# Revit family: ВУТР ПЕ_Eng
name_source: partatom
category: Mechanical Equipment
units: mm (PartAtom-declared; Revit-internal decimal feet)

## family parameters
Always vertical = Yes
Classification = None
Cut with Voids When Loaded = No
Part Type = Normal
Room Calculation Point = No
Round Connector Dimension = Use Diameter
Shared = No
Work Plane-Based = No

## types (20) — shared parameters
00_20_Manufacturer = Vents
00_20_Name = Air handling unit
An = 120 mm  [stored 0.393701 ft]
Casing Material = Steel, galvanized
D1 = 125 mm  [stored 0.410105 ft]
D1y = 120 mm  [stored 0.393701 ft]
Description = Heat- and sound-insulated casing
Filter = G4/G4, F7
Frequency = 50 Hz
Hz = 113 mm
Load Classification = HVAC
Maintenance zone material = <By Category>
Manufacturer = Vents
Number of Fase = 1
Temperature of moving air = -25...+40 °C
URL = https://ventilation-system.com
Voltage = 230 V
d = 8 mm  [stored 0.0262467 ft]
t = 2 mm  [stored 0.00656168 ft]
zero-valued in all types: Default Elevation

## per-type parameters (varying)
- VUTR 250 PE EC L А21: A=1100 mm; A1=1003 mm; Ae=221 mm; Amperage=4 A; Apparent Load=943 VA; Az=251 mm; B=688 mm; B1=643 mm; D=160 mm  [stored 0.524934 ft]; Dy=155 mm  [stored 0.50853 ft]; H=345 mm; Height=345 mm; Hn=230 mm  [stored 0.754593 ft]; L=184 mm  [stored 0.603675 ft]; L2=149 mm  [stored 0.488845 ft]; L3=143 mm; L4=156 mm  [stored 0.511811 ft]; L5=175 mm  [stored 0.574147 ft]; L7=224 mm  [stored 0.734908 ft]; L8=156 mm  [stored 0.511811 ft]; L9=170 mm  [stored 0.557743 ft]; Length=1100 mm; Maximum Air Flow=310.0 m³/h; Power=835 W; Right=No; Sound pressure level at 3 m distance=21 dBA; Weight=56.00 kg; Width=688 mm
- VUTR 250 PE EC R А21: A=1100 mm; A1=1003 mm; Ae=221 mm; Amperage=4 A; Apparent Load=943 VA; Az=825 mm; B=688 mm; B1=643 mm; D=160 mm  [stored 0.524934 ft]; Dy=155 mm  [stored 0.50853 ft]; H=345 mm; Height=345 mm; Hn=230 mm  [stored 0.754593 ft]; L=184 mm  [stored 0.603675 ft]; L2=149 mm  [stored 0.488845 ft]; L3=143 mm; L4=156 mm  [stored 0.511811 ft]; L5=175 mm  [stored 0.574147 ft]; L7=224 mm  [stored 0.734908 ft]; L8=156 mm  [stored 0.511811 ft]; L9=170 mm  [stored 0.557743 ft]; Length=1100 mm; Maximum Air Flow=310.0 m³/h; Power=835 W; Right=Yes; Sound pressure level at 3 m distance=21 dBA; Weight=56.00 kg; Width=688 mm
- VUTR 250 P EC R А21: A=1100 mm; A1=1003 mm; Ae=221 mm; Amperage=1 A; Apparent Load=230 VA; Az=825 mm; B=688 mm; B1=643 mm; D=160 mm  [stored 0.524934 ft]; Dy=155 mm  [stored 0.50853 ft]; H=345 mm; Height=345 mm; Hn=230 mm  [stored 0.754593 ft]; L=184 mm  [stored 0.603675 ft]; L2=149 mm  [stored 0.488845 ft]; L3=143 mm; L4=156 mm  [stored 0.511811 ft]; L5=175 mm  [stored 0.574147 ft]; L7=224 mm  [stored 0.734908 ft]; L8=156 mm  [stored 0.511811 ft]; L9=170 mm  [stored 0.557743 ft]; Length=1100 mm; Maximum Air Flow=310.0 m³/h; Power=135 W; Right=Yes; Sound pressure level at 3 m distance=21 dBA; Weight=55.00 kg; Width=688 mm
- VUTR 250 P EC L А21: A=1100 mm; A1=1003 mm; Ae=221 mm; Amperage=1 A; Apparent Load=230 VA; Az=251 mm; B=688 mm; B1=643 mm; D=160 mm  [stored 0.524934 ft]; Dy=155 mm  [stored 0.50853 ft]; H=345 mm; Height=345 mm; Hn=230 mm  [stored 0.754593 ft]; L=184 mm  [stored 0.603675 ft]; L2=149 mm  [stored 0.488845 ft]; L3=143 mm; L4=156 mm  [stored 0.511811 ft]; L5=175 mm  [stored 0.574147 ft]; L7=224 mm  [stored 0.734908 ft]; L8=156 mm  [stored 0.511811 ft]; L9=170 mm  [stored 0.557743 ft]; Length=1100 mm; Maximum Air Flow=310.0 m³/h; Power=135 W; Right=No; Sound pressure level at 3 m distance=21 dBA; Weight=55.00 kg; Width=688 mm
- VUTR 250 P2 EC L А21: A=1097 mm; A1=1002 mm; Ae=221 mm; Amperage=1 A; Apparent Load=207 VA; Az=251 mm; B=666 mm; B1=618 mm; D=160 mm  [stored 0.524934 ft]; Dy=155 mm  [stored 0.50853 ft]; H=245 mm; Height=245 mm; Hn=163 mm; L=162 mm  [stored 0.531496 ft]; L2=118 mm; L3=111 mm; L4=120 mm  [stored 0.393701 ft]; L5=167 mm  [stored 0.5479 ft]; L7=212 mm  [stored 0.695538 ft]; L8=123 mm  [stored 0.403543 ft]; L9=127 mm; Length=1097 mm; Maximum Air Flow=300.0 m³/h; Power=128 W; Right=No; Sound pressure level at 3 m distance=23 dBA; Weight=53.00 kg; Width=666 mm
- VUTR 250 P2 EC R А21: A=1097 mm; A1=1002 mm; Ae=221 mm; Amperage=1 A; Apparent Load=207 VA; Az=824 mm; B=666 mm; B1=618 mm; D=160 mm  [stored 0.524934 ft]; Dy=155 mm  [stored 0.50853 ft]; H=245 mm; Height=245 mm; Hn=163 mm; L=162 mm  [stored 0.531496 ft]; L2=118 mm; L3=111 mm; L4=120 mm  [stored 0.393701 ft]; L5=167 mm  [stored 0.5479 ft]; L7=212 mm  [stored 0.695538 ft]; L8=123 mm  [stored 0.403543 ft]; L9=127 mm; Length=1097 mm; Maximum Air Flow=300.0 m³/h; Power=128 W; Right=Yes; Sound pressure level at 3 m distance=23 dBA; Weight=53.00 kg; Width=666 mm
- VUTR 250 P2E EC R А21: A=1097 mm; A1=1002 mm; Ae=221 mm; Amperage=4 A; Apparent Load=920 VA; Az=824 mm; B=666 mm; B1=618 mm; D=160 mm  [stored 0.524934 ft]; Dy=155 mm  [stored 0.50853 ft]; H=245 mm; Height=245 mm; Hn=163 mm; L=162 mm  [stored 0.531496 ft]; L2=118 mm; L3=111 mm; L4=120 mm  [stored 0.393701 ft]; L5=167 mm  [stored 0.5479 ft]; L7=212 mm  [stored 0.695538 ft]; L8=123 mm  [stored 0.403543 ft]; L9=127 mm; Length=1097 mm; Maximum Air Flow=300.0 m³/h; Power=828 W; Right=Yes; Sound pressure level at 3 m distance=23 dBA; Weight=54.00 kg; Width=666 mm
- VUTR 250 P2E EC L А21: A=1097 mm; A1=1002 mm; Ae=221 mm; Amperage=4 A; Apparent Load=920 VA; Az=251 mm; B=666 mm; B1=618 mm; D=160 mm  [stored 0.524934 ft]; Dy=155 mm  [stored 0.50853 ft]; H=245 mm; Height=245 mm; Hn=163 mm; L=162 mm  [stored 0.531496 ft]; L2=118 mm; L3=111 mm; L4=120 mm  [stored 0.393701 ft]; L5=167 mm  [stored 0.5479 ft]; L7=212 mm  [stored 0.695538 ft]; L8=123 mm  [stored 0.403543 ft]; L9=127 mm; Length=1097 mm; Maximum Air Flow=300.0 m³/h; Power=828 W; Right=No; Sound pressure level at 3 m distance=23 dBA; Weight=54.00 kg; Width=666 mm
- VUTR 350 P EC L А21: A=1365 mm; A1=1270 mm; Ae=288 mm; Amperage=1 A; Apparent Load=299 VA; Az=318 mm; B=818 mm; B1=770 mm; D=160 mm  [stored 0.524934 ft]; Dy=155 mm  [stored 0.50853 ft]; H=361 mm; Height=361 mm; Hn=241 mm; L=206 mm  [stored 0.675853 ft]; L2=147 mm  [stored 0.482283 ft]; L3=141 mm; L4=160 mm  [stored 0.524934 ft]; L5=207 mm  [stored 0.679134 ft]; L7=287 mm; L8=160 mm  [stored 0.524934 ft]; L9=201 mm  [stored 0.659449 ft]; Length=1365 mm; Maximum Air Flow=430.0 m³/h; Power=185 W; Right=No; Sound pressure level at 3 m distance=31 dBA; Weight=81.00 kg; Width=818 mm
- VUTR 350 P EC R А21: A=1365 mm; A1=1270 mm; Ae=288 mm; Amperage=1 A; Apparent Load=299 VA; Az=1025 mm; B=818 mm; B1=770 mm; D=160 mm  [stored 0.524934 ft]; Dy=155 mm  [stored 0.50853 ft]; H=361 mm; Height=361 mm; Hn=241 mm; L=206 mm  [stored 0.675853 ft]; L2=147 mm  [stored 0.482283 ft]; L3=141 mm; L4=160 mm  [stored 0.524934 ft]; L5=207 mm  [stored 0.679134 ft]; L7=287 mm; L8=160 mm  [stored 0.524934 ft]; L9=201 mm  [stored 0.659449 ft]; Length=1365 mm; Maximum Air Flow=430.0 m³/h; Power=185 W; Right=Yes; Sound pressure level at 3 m distance=31 dBA; Weight=81.00 kg; Width=818 mm
- VUTR 350 PE EC R А21: A=1365 mm; A1=1270 mm; Ae=288 mm; Amperage=7 A; Apparent Load=1587 VA; Az=1025 mm; B=818 mm; B1=770 mm; D=160 mm  [stored 0.524934 ft]; Dy=155 mm  [stored 0.50853 ft]; H=361 mm; Height=361 mm; Hn=241 mm; L=206 mm  [stored 0.675853 ft]; L2=147 mm  [stored 0.482283 ft]; L3=141 mm; L4=160 mm  [stored 0.524934 ft]; L5=207 mm  [stored 0.679134 ft]; L7=287 mm; L8=160 mm  [stored 0.524934 ft]; L9=201 mm  [stored 0.659449 ft]; Length=1365 mm; Maximum Air Flow=430.0 m³/h; Power=1585 W; Right=Yes; Sound pressure level at 3 m distance=31 dBA; Weight=82.00 kg; Width=818 mm
- VUTR 350 PE EC L А21: A=1365 mm; A1=1270 mm; Ae=288 mm; Amperage=7 A; Apparent Load=1587 VA; Az=318 mm; B=818 mm; B1=770 mm; D=160 mm  [stored 0.524934 ft]; Dy=155 mm  [stored 0.50853 ft]; H=361 mm; Height=361 mm; Hn=241 mm; L=206 mm  [stored 0.675853 ft]; L2=147 mm  [stored 0.482283 ft]; L3=141 mm; L4=160 mm  [stored 0.524934 ft]; L5=207 mm  [stored 0.679134 ft]; L7=287 mm; L8=160 mm  [stored 0.524934 ft]; L9=201 mm  [stored 0.659449 ft]; Length=1365 mm; Maximum Air Flow=430.0 m³/h; Power=1585 W; Right=No; Sound pressure level at 3 m distance=31 dBA; Weight=82.00 kg; Width=818 mm
- VUTR 350 P2 EC L А21: A=1457 mm; A1=1362 mm; Ae=311 mm; Amperage=1 A; Apparent Load=299 VA; Az=341 mm; B=847 mm; B1=798 mm; D=160 mm  [stored 0.524934 ft]; Dy=155 mm  [stored 0.50853 ft]; H=245 mm; Height=245 mm; Hn=163 mm; L=209 mm  [stored 0.685696 ft]; L2=155 mm  [stored 0.50853 ft]; L3=117 mm  [stored 0.383858 ft]; L4=126 mm  [stored 0.413386 ft]; L5=223 mm  [stored 0.731627 ft]; L7=274 mm; L8=120 mm  [stored 0.393701 ft]; L9=126 mm  [stored 0.413386 ft]; Length=1457 mm; Maximum Air Flow=400.0 m³/h; Power=200 W; Right=No; Sound pressure level at 3 m distance=33 dBA; Weight=78.00 kg; Width=847 mm
- VUTR 350 P2 EC R А21: A=1457 mm; A1=1362 mm; Ae=311 mm; Amperage=1 A; Apparent Load=299 VA; Az=1094 mm; B=847 mm; B1=798 mm; D=160 mm  [stored 0.524934 ft]; Dy=155 mm  [stored 0.50853 ft]; H=245 mm; Height=245 mm; Hn=163 mm; L=209 mm  [stored 0.685696 ft]; L2=155 mm  [stored 0.50853 ft]; L3=117 mm  [stored 0.383858 ft]; L4=126 mm  [stored 0.413386 ft]; L5=223 mm  [stored 0.731627 ft]; L7=274 mm; L8=120 mm  [stored 0.393701 ft]; L9=126 mm  [stored 0.413386 ft]; Length=1457 mm; Maximum Air Flow=400.0 m³/h; Power=200 W; Right=Yes; Sound pressure level at 3 m distance=33 dBA; Weight=78.00 kg; Width=847 mm
- VUTR 350 P2E EC L А21: A=1457 mm; A1=1362 mm; Ae=311 mm; Amperage=7 A; Apparent Load=1587 VA; Az=341 mm; B=847 mm; B1=798 mm; D=160 mm  [stored 0.524934 ft]; Dy=155 mm  [stored 0.50853 ft]; H=245 mm; Height=245 mm; Hn=163 mm; L=209 mm  [stored 0.685696 ft]; L2=155 mm  [stored 0.50853 ft]; L3=117 mm  [stored 0.383858 ft]; L4=126 mm  [stored 0.413386 ft]; L5=223 mm  [stored 0.731627 ft]; L7=274 mm; L8=120 mm  [stored 0.393701 ft]; L9=126 mm  [stored 0.413386 ft]; Length=1457 mm; Maximum Air Flow=400.0 m³/h; Power=1600 W; Right=No; Sound pressure level at 3 m distance=33 dBA; Weight=79.00 kg; Width=847 mm
- VUTR 350 P2E EC R А21: A=1457 mm; A1=1362 mm; Ae=311 mm; Amperage=7 A; Apparent Load=1587 VA; Az=341 mm; B=847 mm; B1=798 mm; D=160 mm  [stored 0.524934 ft]; Dy=155 mm  [stored 0.50853 ft]; H=245 mm; Height=245 mm; Hn=163 mm; L=209 mm  [stored 0.685696 ft]; L2=155 mm  [stored 0.50853 ft]; L3=117 mm  [stored 0.383858 ft]; L4=126 mm  [stored 0.413386 ft]; L5=223 mm  [stored 0.731627 ft]; L7=274 mm; L8=120 mm  [stored 0.393701 ft]; L9=126 mm  [stored 0.413386 ft]; Length=1457 mm; Maximum Air Flow=400.0 m³/h; Power=1600 W; Right=No; Sound pressure level at 3 m distance=33 dBA; Weight=79.00 kg; Width=847 mm
- VUTR 650 P EC R А21: A=1542 mm; A1=1445 mm; Ae=331 mm; Amperage=3 A; Apparent Load=575 VA; Az=1156 mm; B=932 mm; B1=897 mm; D=200 mm  [stored 0.656168 ft]; Dy=195 mm  [stored 0.639764 ft]; H=422 mm; Height=422 mm; Hn=281 mm; L=317 mm; L2=229 mm; L3=195 mm  [stored 0.639764 ft]; L4=203 mm  [stored 0.66601 ft]; L5=172 mm  [stored 0.564304 ft]; L7=231 mm; L8=207 mm  [stored 0.679134 ft]; L9=219 mm  [stored 0.718504 ft]; Length=1542 mm; Maximum Air Flow=710.0 m³/h; Power=367 W; Right=Yes; Sound pressure level at 3 m distance=36 dBA; Weight=102.00 kg; Width=932 mm
- VUTR 650 P EC L А21: A=1542 mm; A1=1445 mm; Ae=331 mm; Amperage=3 A; Apparent Load=575 VA; Az=361 mm; B=932 mm; B1=897 mm; D=200 mm  [stored 0.656168 ft]; Dy=195 mm  [stored 0.639764 ft]; H=422 mm; Height=422 mm; Hn=281 mm; L=317 mm; L2=229 mm; L3=195 mm  [stored 0.639764 ft]; L4=203 mm  [stored 0.66601 ft]; L5=172 mm  [stored 0.564304 ft]; L7=231 mm; L8=207 mm  [stored 0.679134 ft]; L9=219 mm  [stored 0.718504 ft]; Length=1542 mm; Maximum Air Flow=710.0 m³/h; Power=367 W; Right=No; Sound pressure level at 3 m distance=36 dBA; Weight=102.00 kg; Width=932 mm
- VUTR 650 PE EC L А21: A=1542 mm; A1=1445 mm; Ae=331 mm; Amperage=14 A; Apparent Load=3151 VA; Az=361 mm; B=932 mm; B1=897 mm; D=200 mm  [stored 0.656168 ft]; Dy=195 mm  [stored 0.639764 ft]; H=422 mm; Height=422 mm; Hn=281 mm; L=317 mm; L2=229 mm; L3=195 mm  [stored 0.639764 ft]; L4=203 mm  [stored 0.66601 ft]; L5=172 mm  [stored 0.564304 ft]; L7=231 mm; L8=207 mm  [stored 0.679134 ft]; L9=219 mm  [stored 0.718504 ft]; Length=1542 mm; Maximum Air Flow=710.0 m³/h; Power=3167 W; Right=No; Sound pressure level at 3 m distance=36 dBA; Weight=104.00 kg; Width=932 mm
- VUTR 650 PE EC R А21: A=1542 mm; A1=1445 mm; Ae=331 mm; Amperage=14 A; Apparent Load=3151 VA; Az=1156 mm; B=932 mm; B1=897 mm; D=200 mm  [stored 0.656168 ft]; Dy=195 mm  [stored 0.639764 ft]; H=422 mm; Height=422 mm; Hn=281 mm; L=317 mm; L2=229 mm; L3=195 mm  [stored 0.639764 ft]; L4=203 mm  [stored 0.66601 ft]; L5=172 mm  [stored 0.564304 ft]; L7=231 mm; L8=207 mm  [stored 0.679134 ft]; L9=219 mm  [stored 0.718504 ft]; Length=1542 mm; Maximum Air Flow=710.0 m³/h; Power=3167 W; Right=Yes; Sound pressure level at 3 m distance=36 dBA; Weight=104.00 kg; Width=932 mm

note: column(s) folded — value = type name in every type: 00_20_Type

note: [stored X ft] marks values corroborated as IEEE doubles in the binary element streams (Revit-internal decimal feet)
